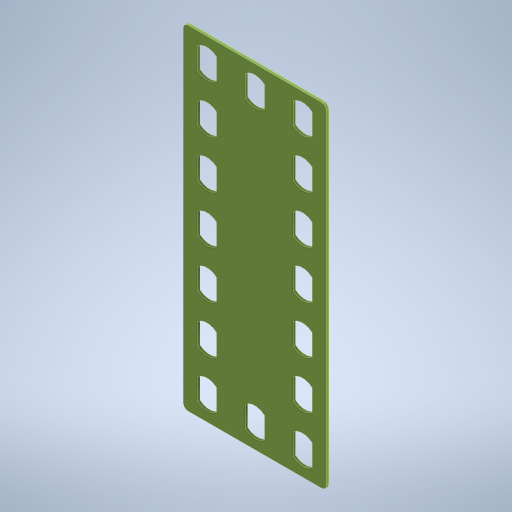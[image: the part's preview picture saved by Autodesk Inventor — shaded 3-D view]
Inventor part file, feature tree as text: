
AUTODESK INVENTOR PART (.ipt)
format: ipt  version: 2024 (Build 280153000, 153)  size: 357,888 bytes
history: native  units: mm
features: pattern_linear x4, extrude x3, fillet x3, sketch x3, other x1
ambient origin geometry x8: Origin, YZ Plane, XZ Plane, XY Plane, X Axis, Y Axis, Z Axis, Center Point
bodies: Body1 (feature_tree)
feature tree (14):
  other  "Těleso1"
  extrude  "Vysunutí1"  Depth=70.0mm
  fillet  "Zaoblení1"  Radius=30.0mm
  fillet  "Zaoblení2"  Radius=10.0mm
  fillet  "Zaoblení3"  Radius=10.0mm
  extrude  "Vysunutí3"  Depth=0.5mm TaperAngle=0.0deg
  pattern_linear  "Obdélníkové pole2"  Spacing1=1.0mm  [1 undecoded]
  pattern_linear  "Obdélníkové pole3"  Spacing1=1.0mm  [1 undecoded]
  extrude  "Vysunutí4"  Depth=1.0mm
  pattern_linear  "Obdélníkové pole4"  Spacing1=2.0mm  [1 undecoded]
  pattern_linear  "Obdélníkové pole5"  Spacing1=5.0mm  [1 undecoded]
  sketch  "Náčrt1"
  sketch  "Náčrt3"
  sketch  "Náčrt4"
note: 4 required parameter values undecoded (feature->parameter linkage not recoverable at this tier; creation-order binding heuristic only, values carry confidence <= 0.55)
